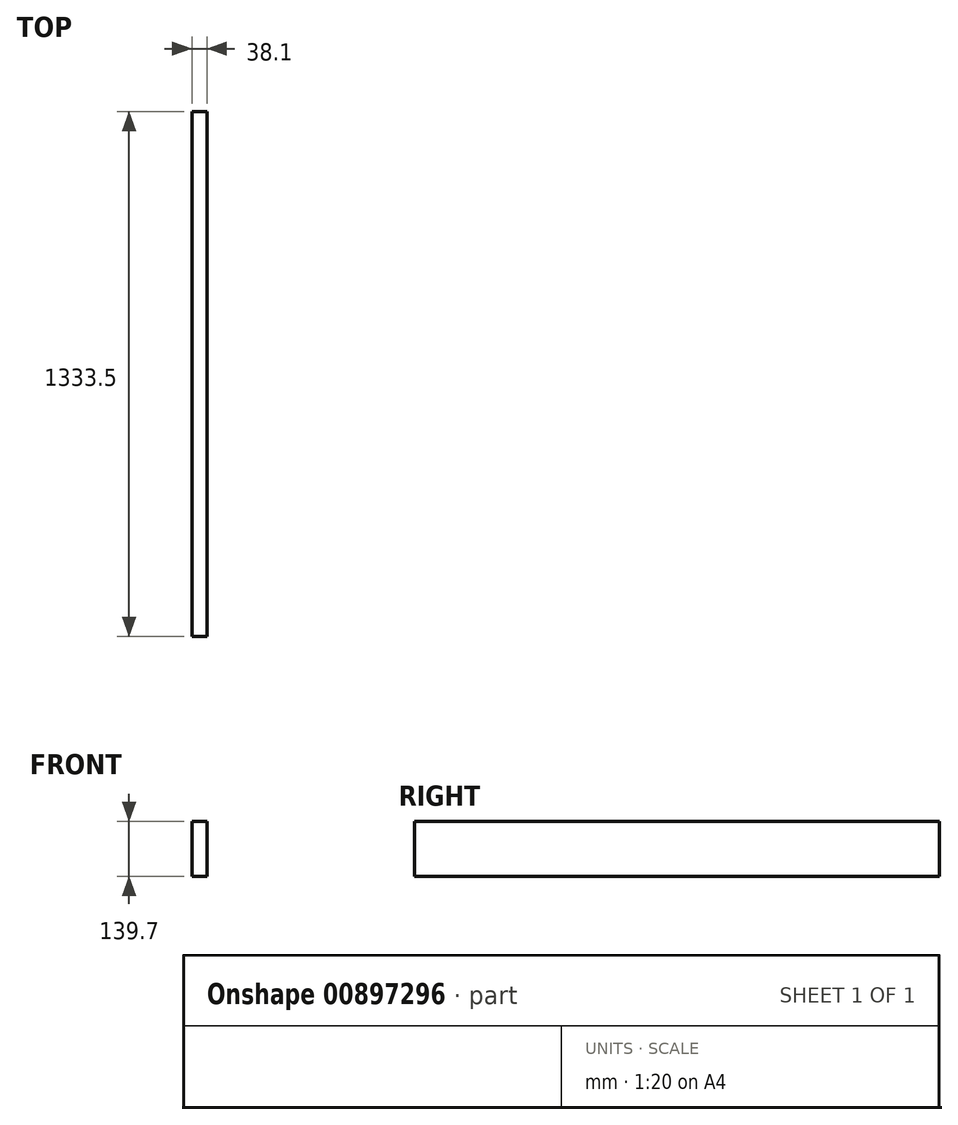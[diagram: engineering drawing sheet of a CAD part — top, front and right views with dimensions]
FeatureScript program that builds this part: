
annotation { "Feature Type Name" : "Feature", "Feature Type Description" : "" }
export const myFeature = defineFeature(function(context is Context, id is Id, definition is map)
    precondition{}
    {
        {
            var Q0;
            Q0=qCreatedBy(makeId("Front.planeOp"),FACE);
            var sketch = newSketch(context, id + "F0", { "sketchPlane" : qUnion([Q0])});
            skLineSegment(sketch, "E0.bottom", {"start": v(-34.3, 91.86) * mm, "end": v(3.8, 91.86) * mm});
            skLineSegment(sketch, "E0.top", {"start": v(-34.3, -47.84) * mm, "end": v(3.8, -47.84) * mm});
            skLineSegment(sketch, "E0.left", {"start": v(-34.3, 91.86) * mm, "end": v(-34.3, -47.84) * mm});
            skLineSegment(sketch, "E0.right", {"start": v(3.8, 91.86) * mm, "end": v(3.8, -47.84) * mm});
            skSolve(sketch);
        }
        {
            var Q0;
            Q0=makeQuery(id+"F0.imprint","IMPRINT",FACE,{"disambiguationData":[TD([[makeQuery(id+"F0.imprint","IMPRINT",EDGE,{"derivedFrom":sQuery(id+"F0.wireOp",EDGE,"E0.bottom")}),-1.0]])]});
            extrude(context, id + "F1", {"entities" : qUnion([Q0]), "depth" : 1333.5 * mm, "offsetDistance" : 25.4 * mm});
        }
    });
